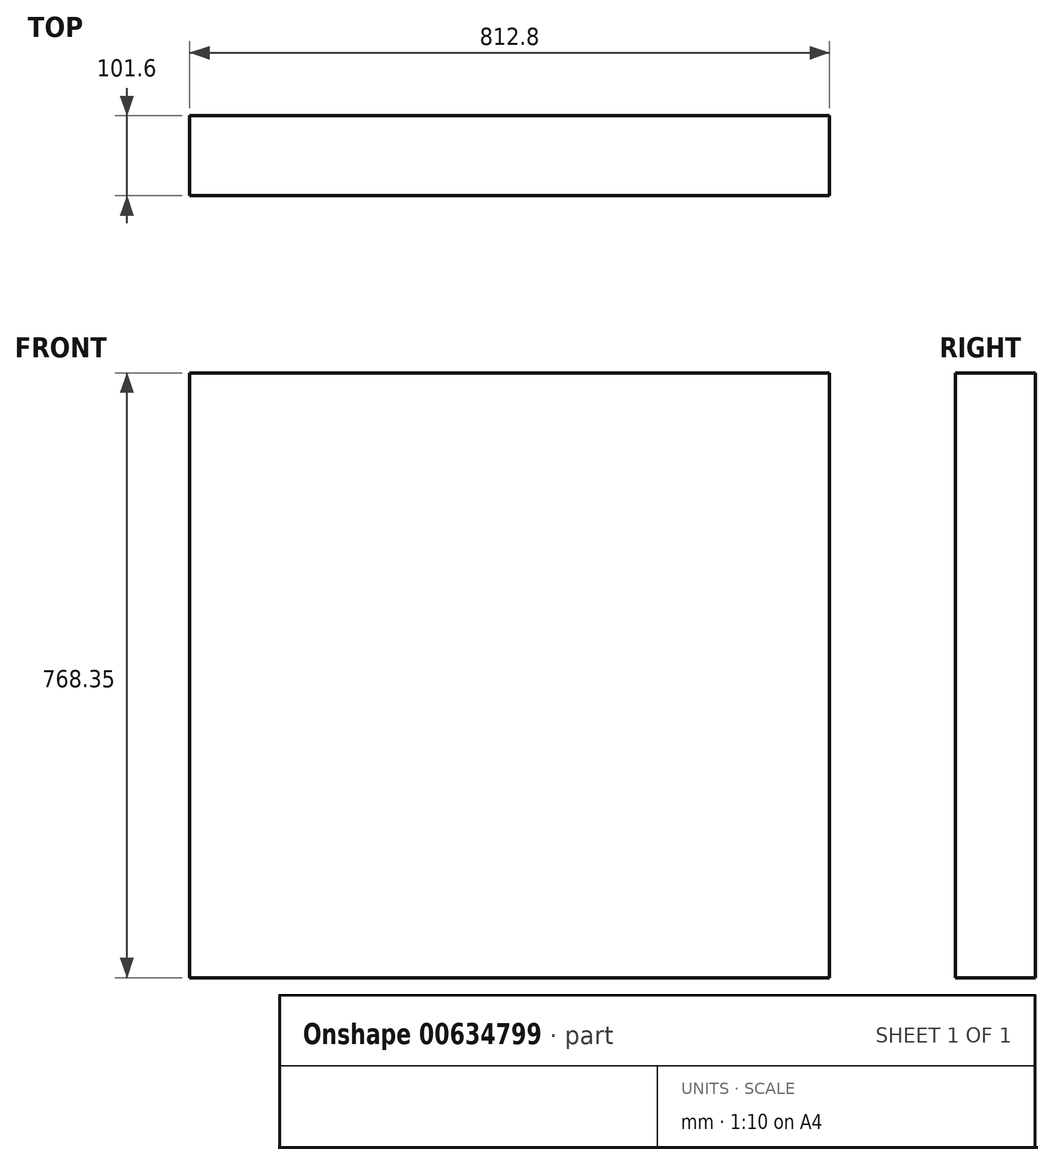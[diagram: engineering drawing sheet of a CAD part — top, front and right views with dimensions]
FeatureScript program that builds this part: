
annotation { "Feature Type Name" : "Feature", "Feature Type Description" : "" }
export const myFeature = defineFeature(function(context is Context, id is Id, definition is map)
    precondition{}
    {
        {
            var Q0;
            Q0=qCreatedBy(makeId("Right.planeOp"),FACE);
            var sketch = newSketch(context, id + "F0", { "sketchPlane" : qUnion([Q0])});
            skLineSegment(sketch, "E0.bottom", {"start": v(47.46, 667.55) * mm, "end": v(-54.14, 667.55) * mm});
            skLineSegment(sketch, "E0.top", {"start": v(47.46, -100.8) * mm, "end": v(-54.14, -100.8) * mm});
            skLineSegment(sketch, "E0.left", {"start": v(47.46, 667.55) * mm, "end": v(47.46, -100.8) * mm});
            skLineSegment(sketch, "E0.right", {"start": v(-54.14, 667.55) * mm, "end": v(-54.14, -100.8) * mm});
            skSolve(sketch);
        }
        {
            var Q0;
            Q0 = qSketchRegion(id + "F0", true);
            extrude(context, id + "F1", {"entities" : qUnion([Q0]), "depth" : 812.8 * mm, "offsetDistance" : 25.4 * mm});
        }
    });
